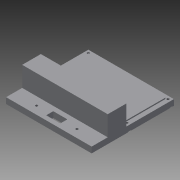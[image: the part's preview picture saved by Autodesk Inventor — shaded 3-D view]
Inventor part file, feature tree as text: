
AUTODESK INVENTOR PART (.ipt)
format: ipt  version: 2015 (Build 190159000, 159)  size: 153,600 bytes
history: native  units: mm
features: sketch x6, extrude x5, hole x1
ambient origin geometry x8: Origin, YZ Plane, XZ Plane, XY Plane, X Axis, Y Axis, Z Axis, Center Point
bodies: Solid1 (feature_tree)
feature tree (12):
  extrude  "Extrusion1"  Depth=70.0mm
  extrude  "Extrusion13"  Depth=3.7mm
  hole  "Hole2"  [1 undecoded]
  extrude  "Extrusion16"  Depth=1.0mm
  extrude  "Extrusion17"  Depth=2.0mm
  extrude  "Extrusion18"  Depth=30.4mm
  sketch  "Sketch1"  dims[d0=72.8mm d1=70.0mm]
  sketch  "Sketch14"  dims[d6=5.0mm d7=0.0mm d92=3.7mm]
  sketch  "Sketch15"  dims[d93=3.7mm d94=3.7mm]
  sketch  "Sketch18"  dims[d97=1.0mm d98=0.0mm d99=32.8mm]
  sketch  "Sketch19"  dims[d100=2.0mm d101=2.5mm]
  sketch  "Sketch20"  dims[d102=2.5mm d103=40.0mm d104=20.0mm d105=2.0mm d106=6.0mm d107=6.0mm d108=2.0mm d109=90.0deg d110=6.0mm d111=20.594885mm d123=3.9mm d124=13.7mm d125=17.0mm d126=0.0mm d127=2.0mm d128=2.0mm d129=6.75mm d130=6.75mm d131=17.2mm d132=17.2mm d133=15.0mm d134=0.0mm d135=12.0mm d136=6.0mm d137=3.75mm d138=30.4mm d139=15.0mm d140=0.0mm]
note: 1 required parameter value undecoded (feature->parameter linkage not recoverable at this tier; creation-order binding heuristic only, values carry confidence <= 0.55)
